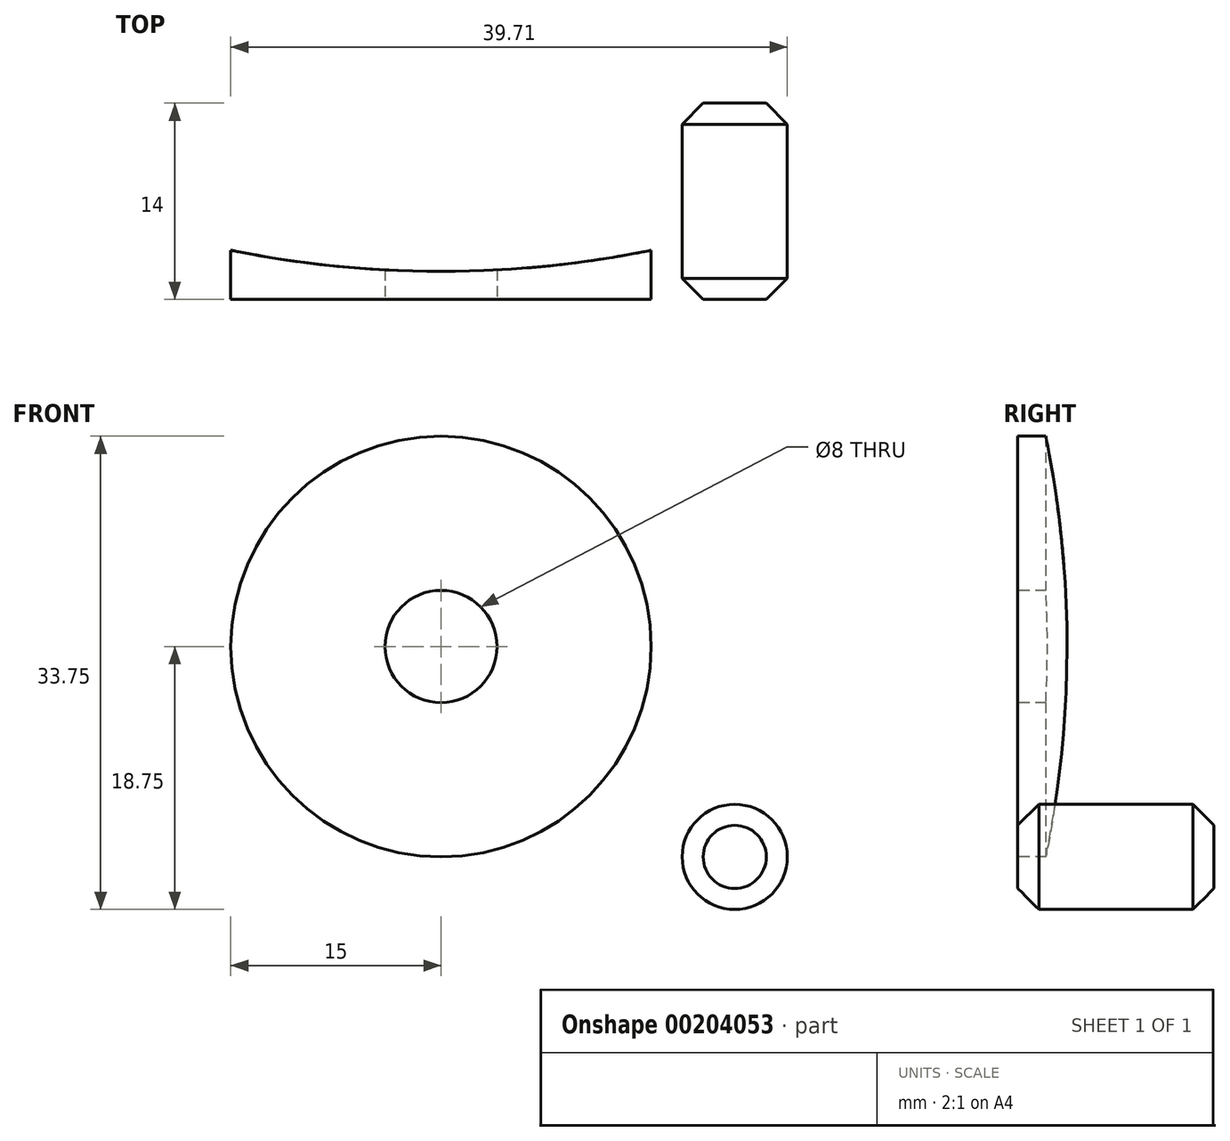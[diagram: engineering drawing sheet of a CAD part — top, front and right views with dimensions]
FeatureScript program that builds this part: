
annotation { "Feature Type Name" : "Feature", "Feature Type Description" : "" }
export const myFeature = defineFeature(function(context is Context, id is Id, definition is map)
    precondition{}
    {
        {
            var Q0;
            Q0=qCreatedBy(makeId("Top.planeOp"),FACE);
            var sketch = newSketch(context, id + "F0", { "sketchPlane" : qUnion([Q0])});
            skCircle(sketch, "E0", {"center": v(0, 0) * mm, "radius": 75 * mm});
            skSolve(sketch);
        }
        {
            var Q0;
            Q0=qCreatedBy(makeId("Front.planeOp"),FACE);
            cPlane(context, id + "F1", {"entities" : qUnion([Q0]), "cplaneType" : CPlaneType.OFFSET, "offset" : 77 * mm, "width" : 150 * mm, "height" : 150 * mm});
        }
        {
            var Q0;
            Q0=qCreatedBy(id+"F1.planeOp",FACE);
            var sketch = newSketch(context, id + "F2", { "sketchPlane" : qUnion([Q0])});
            skCircle(sketch, "E1", {"center": v(0, 15) * mm, "radius": 15 * mm});
            skSolve(sketch);
        }
        {
            var Q0;
            Q0=makeQuery(id+"F2.imprint","IMPRINT",FACE,{"disambiguationData":[TD([[makeQuery(id+"F2.imprint","IMPRINT",EDGE,{"derivedFrom":sQuery(id+"F2.wireOp",EDGE,"E1")}),1.0]])]});
            extrude(context, id + "F3", {"entities" : qUnion([Q0]), "oppositeDirection" : true, "depth" : 5 * mm});
        }
        {
            var Q0;
            Q0=makeQuery(id+"F0.imprint","IMPRINT",FACE,{"disambiguationData":[TD([[makeQuery(id+"F0.imprint","IMPRINT",EDGE,{"derivedFrom":sQuery(id+"F0.wireOp",EDGE,"E0")}),1.0]])]});
            extrude(context, id + "F4", {"entities" : qUnion([Q0]), "operationType" : NewBodyOperationType.REMOVE, "depth" : 50 * mm});
        }
        {
            var Q0;
            Q0=makeQuery(id+"F3.opExtrude","CAP_FACE",FACE,{"disambiguationData":[OSD([sQuery(id+"F2.wireOp",EDGE,"E1")])],"isStart":true});
            var sketch = newSketch(context, id + "F5", { "sketchPlane" : qUnion([Q0])});
            skCircle(sketch, "E2", {"center": v(0, 15) * mm, "radius": 4 * mm});
            skSolve(sketch);
        }
        {
            var Q0;
            Q0=makeQuery(id+"F5.imprint","IMPRINT",FACE,{"disambiguationData":[TD([[makeQuery(id+"F5.imprint","IMPRINT",EDGE,{"derivedFrom":sQuery(id+"F5.wireOp",EDGE,"E2")}),1.0]])]});
            var Q1;
            Q1=sQuery(id+"F5.wireOp",EDGE,"E2");
            extrude(context, id + "F6", {"entities" : qUnion([Q0]), "operationType" : NewBodyOperationType.REMOVE, "surfaceEntities" : qUnion([Q1]), "oppositeDirection" : true, "depth" : 25 * mm});
        }
        {
            var Q0;
            Q0=qCreatedBy(id+"F1.planeOp",FACE);
            var sketch = newSketch(context, id + "F7", { "sketchPlane" : qUnion([Q0])});
            skCircle(sketch, "E3", {"center": v(20.96, 0) * mm, "radius": 3.75 * mm});
            skSolve(sketch);
        }
        {
            var Q0;
            Q0=makeQuery(id+"F7.imprint","IMPRINT",FACE,{"disambiguationData":[TD([[makeQuery(id+"F7.imprint","IMPRINT",EDGE,{"derivedFrom":sQuery(id+"F7.wireOp",EDGE,"E3")}),1.0]])]});
            extrude(context, id + "F8", {"entities" : qUnion([Q0]), "oppositeDirection" : true, "depth" : 14 * mm});
        }
        {
            var Q0;
            Q0=makeQuery(id+"F8.opExtrude","CAP_FACE",FACE,{"disambiguationData":[OSD([sQuery(id+"F7.wireOp",EDGE,"E3")])],"isStart":true});
            var Q1;
            Q1=makeQuery(id+"F8.opExtrude","CAP_EDGE",EDGE,{"disambiguationData":[OSD([sQuery(id+"F7.wireOp",EDGE,"E3")])],"isStart":false});
            chamfer(context, id + "F9", {"entities" : qUnion([Q0, Q1]), "width" : 1.5 * mm, "tangentPropagation" : true});
        }
    });
